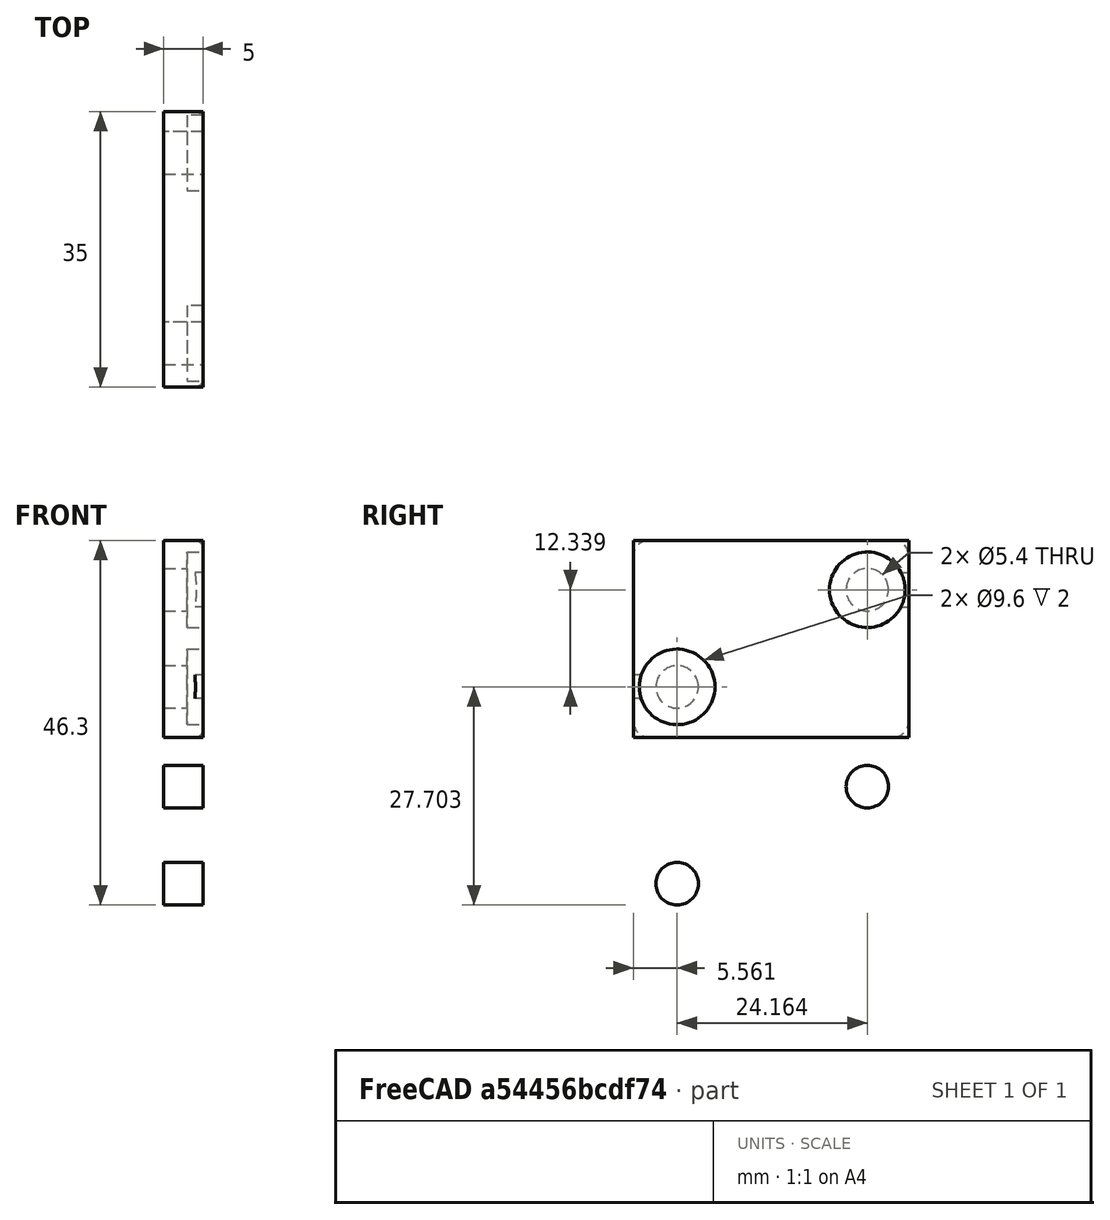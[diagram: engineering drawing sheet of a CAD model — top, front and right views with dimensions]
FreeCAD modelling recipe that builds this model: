
FCSTD DOCUMENT  (FreeCAD 0.16R)
Label: RackClipNut
License: All rights reserved
LicenseURL: http://en.wikipedia.org/wiki/All_rights_reserved
objects: Sketcher::SketchObject×3, PartDesign::Pocket×2, PartDesign::Fillet×2, PartDesign::Pad×1, Mesh::Feature×1
note: 11 computed .brp shape members not serialized (recipe doc carries the construction recipe); baked Part::Feature solids carry a one-line shape summary decoded from their .brp

FEATURE [Sketcher::SketchObject] Sketch002
  Placement = pos=(0,0,25) rot=(0,0,1;0rad)
  sketch-geometry (4):
    g0: LineSegment StartX=0 StartY=35 StartZ=0 EndX=5 EndY=35 EndZ=0
    g1: LineSegment StartX=5 StartY=35 StartZ=0 EndX=5 EndY=0 EndZ=0
    g2: LineSegment StartX=5 StartY=0 StartZ=0 EndX=0 EndY=0 EndZ=0
    g3: LineSegment StartX=0 StartY=0 StartZ=0 EndX=0 EndY=35 EndZ=0
  constraints (11):
    c: Coincident(g0,g1)
    c: Coincident(g1,g2)
    c: Coincident(g2,g3)
    c: Coincident(g3,g0)
    c: Horizontal(g0)
    c: Horizontal(g2)
    c: Vertical(g1)
    c: Vertical(g3)
    c: Distance(g2) = 5
    c: Distance(g1) = 35
    c: Coincident(g2,g-1)
FEATURE [PartDesign::Pad] Pad
  Length = 25
  Length2 = 100
  Placement = pos=(0,0,25) rot=(0,0,1;0rad)
  Sketch = -> Sketch002
  Type = 0
FEATURE [Sketcher::SketchObject] Sketch005
  Placement = pos=(5,0,25) rot=(0.57735,0.57735,0.57735;2.0944rad)
  Support = -> Pad [Face2]
  sketch-geometry (2):
    g0: Circle CenterX=29.7252 CenterY=18.7423 CenterZ=0 NormalX=0 NormalY=0 NormalZ=1 Radius=2.7
    g1: Circle CenterX=5.56076 CenterY=6.40305 CenterZ=0 NormalX=0 NormalY=0 NormalZ=1 Radius=2.7
  constraints (2):
    c: Radius(g0) = 2.7
    c: Equal(g0,g1)
FEATURE [PartDesign::Pocket] Pocket
  Length = 5
  Placement = pos=(0,0,25) rot=(0,0,1;0rad)
  Sketch = -> Sketch005
  Type = 0
FEATURE [Sketcher::SketchObject] Sketch
  ExternalGeometry = -> [Pocket]
  Placement = pos=(5,0,25) rot=(0.57735,0.57735,0.57735;2.0944rad)
  Support = -> Pocket [Face3]
  sketch-geometry (2):
    g0: Circle CenterX=29.7252 CenterY=18.7423 CenterZ=0 NormalX=0 NormalY=0 NormalZ=1 Radius=4.8
    g1: Circle CenterX=5.56076 CenterY=6.40305 CenterZ=0 NormalX=0 NormalY=0 NormalZ=1 Radius=4.8
  constraints (4):
    c: Radius(g1) = 4.8
    c: Equal(g1,g0)
    c: Coincident(g0,g-3)
    c: Coincident(g1,g-4)
FEATURE [PartDesign::Pocket] Pocket001
  Length = 2
  Placement = pos=(0,0,25) rot=(0,0,1;0rad)
  Sketch = -> Sketch
  Type = 0
FEATURE [PartDesign::Fillet] Fillet
  Base = -> Pocket001 [Edge15,Edge3,Edge4,Edge16]
  Placement = pos=(0,0,25) rot=(0,0,1;0rad)
  Radius = 2
FEATURE [PartDesign::Fillet] Fillet001
  Base = -> Fillet [Edge18]
  Placement = pos=(0,0,25) rot=(0,0,1;0rad)
  Radius = 1
FEATURE [Mesh::Feature] Mesh  label="Fillet001 (Meshed)"
